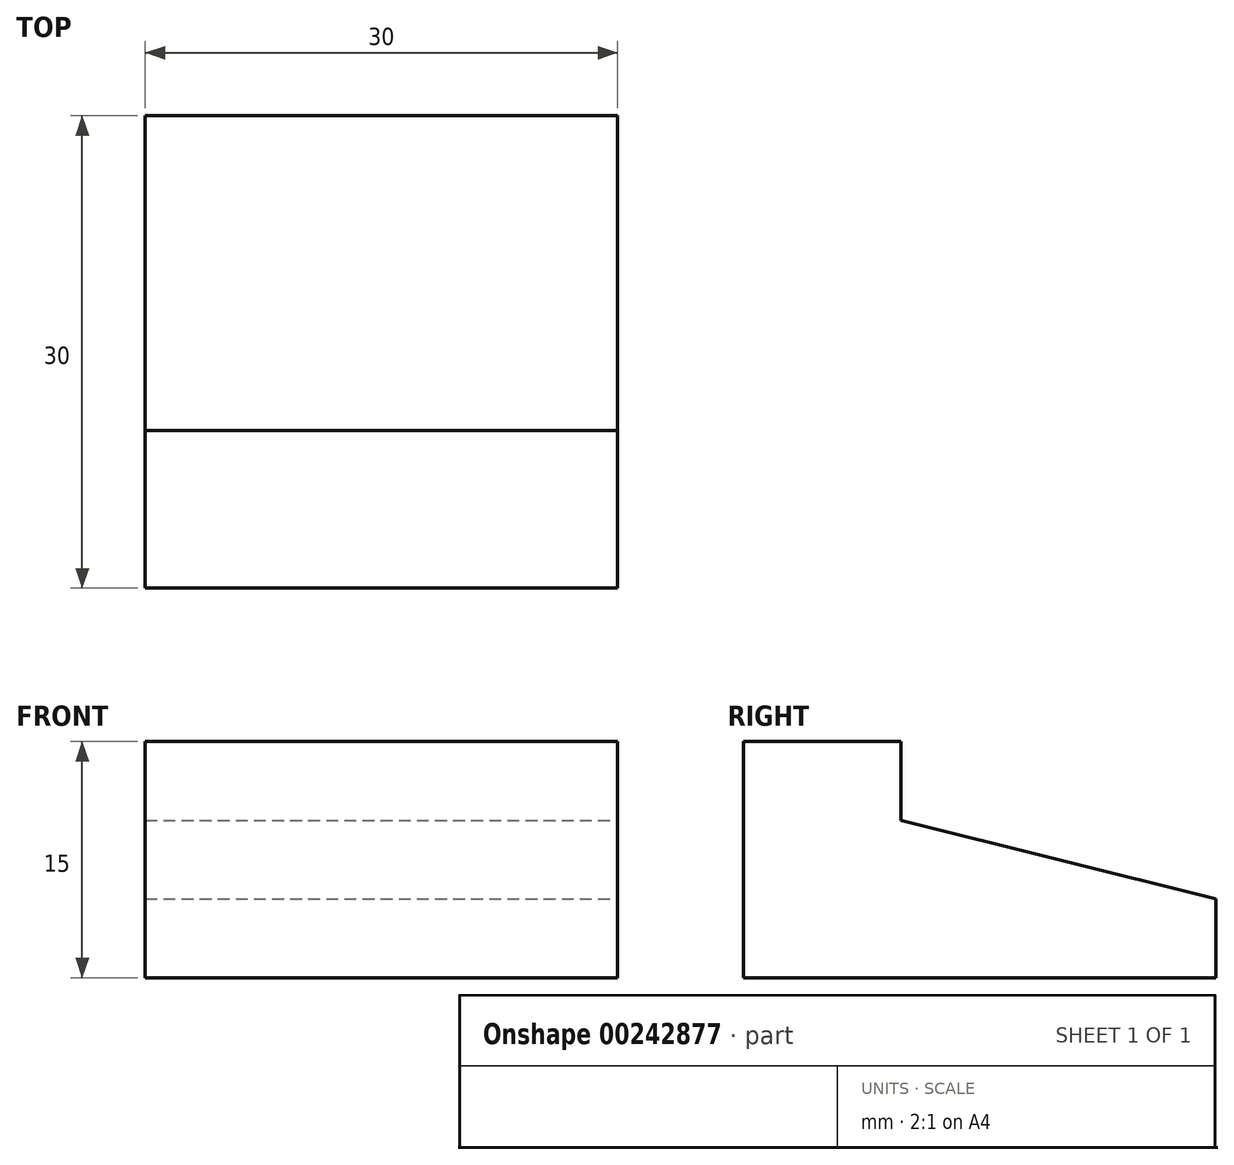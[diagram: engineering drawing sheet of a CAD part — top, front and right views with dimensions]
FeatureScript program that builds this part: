
annotation { "Feature Type Name" : "Feature", "Feature Type Description" : "" }
export const myFeature = defineFeature(function(context is Context, id is Id, definition is map)
    precondition{}
    {
        {
            var Q0;
            Q0=qCreatedBy(makeId("Top.planeOp"),FACE);
            var sketch = newSketch(context, id + "F0", { "sketchPlane" : qUnion([Q0])});
            skLineSegment(sketch, "E0.bottom", {"start": v(-35.55, 29.91) * mm, "end": v(-5.55, 29.91) * mm});
            skLineSegment(sketch, "E0.top", {"start": v(-35.55, -0.09) * mm, "end": v(-5.55, -0.09) * mm});
            skLineSegment(sketch, "E0.left", {"start": v(-35.55, 29.91) * mm, "end": v(-35.55, -0.09) * mm});
            skLineSegment(sketch, "E0.right", {"start": v(-5.55, 29.91) * mm, "end": v(-5.55, -0.09) * mm});
            skSolve(sketch);
        }
        {
            var Q0;
            Q0 = qSketchRegion(id + "F0", true);
            extrude(context, id + "F1", {"entities" : qUnion([Q0]), "depth" : 15 * mm});
        }
        {
            var Q0;
            Q0=makeQuery(id+"F1.opExtrude","SWEPT_FACE",FACE,{"disambiguationData":[OSD([sQuery(id+"F0.wireOp",EDGE,"E0.right")])]});
            var sketch = newSketch(context, id + "F2", { "sketchPlane" : qUnion([Q0])});
            skLineSegment(sketch, "E1", {"start": v(-0.09, 15) * mm, "end": v(9.91, 15) * mm});
            skLineSegment(sketch, "E2", {"start": v(29.91, 0) * mm, "end": v(29.91, 5) * mm});
            skLineSegment(sketch, "E3", {"start": v(9.91, 15) * mm, "end": v(29.91, 5) * mm});
            skLineSegment(sketch, "E4", {"start": v(9.91, 15) * mm, "end": v(9.91, 10) * mm});
            skPoint(sketch, "E4.endSnap0", {"position": v(19.91, 10) * mm});
            skLineSegment(sketch, "E5", {"start": v(9.91, 10) * mm, "end": v(29.91, 5) * mm});
            skSolve(sketch);
        }
        {
            var Q0;
            {var subQ0=sQuery(id+"F2.wireOp",EDGE,"E3");Q0=makeQuery(id+"F2.imprint","IMPRINT",FACE,{"disambiguationData":[TD([[makeQuery(id+"F2.imprint","IMPRINT",EDGE,{"derivedFrom":subQ0}),1.0]])]});}
            var Q1;
            Q1=makeQuery(id+"F2.imprint","IMPRINT",FACE,{"disambiguationData":[TD([[makeQuery(id+"F2.imprint","IMPRINT",EDGE,{"derivedFrom":sQuery(id+"F2.wireOp",EDGE,"E3")}),-1.0]])]});
            extrude(context, id + "F3", {"entities" : qUnion([Q0, Q1]), "operationType" : NewBodyOperationType.REMOVE, "endBound" : BoundingType.THROUGH_ALL, "oppositeDirection" : true, "depth" : 25 * mm});
        }
    });
